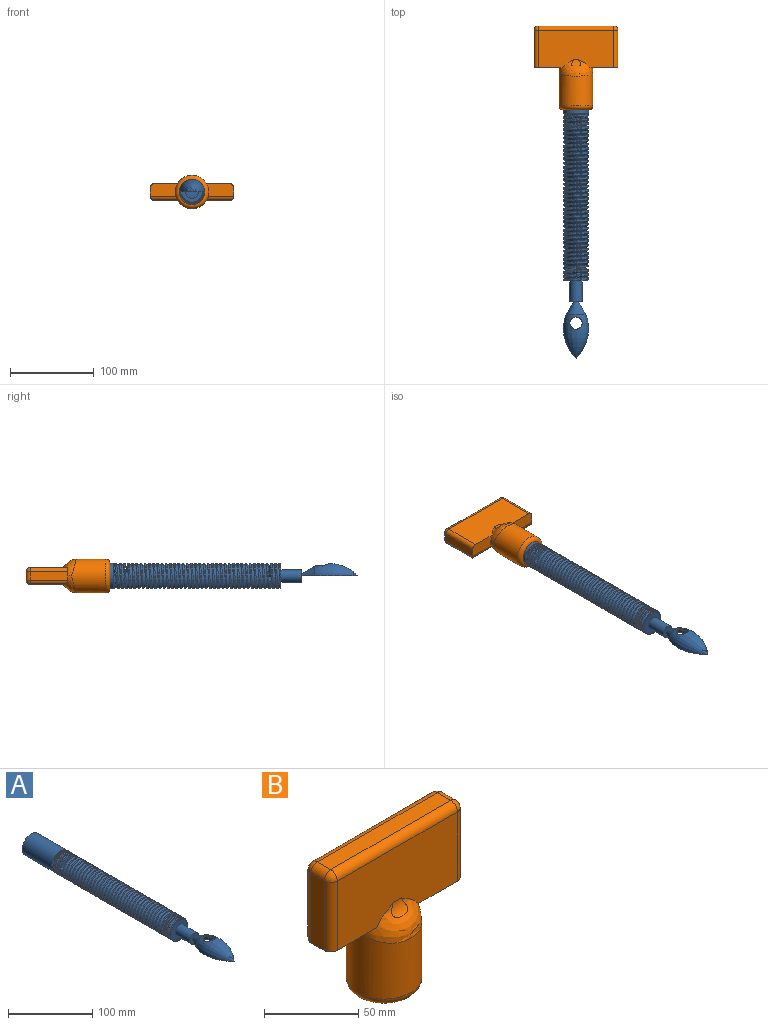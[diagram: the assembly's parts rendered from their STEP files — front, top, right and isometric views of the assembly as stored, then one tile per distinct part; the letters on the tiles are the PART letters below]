
ASSEMBLY  parts=2 mates=2
PART A: 57 faces, bbox 42.2x349.3x47.4 mm
  f0: revolved ~52.11x25.36mm, area 1460.1mm2, adj f53,f54,f55,f56
  f1: revolved ~52.11x29.95mm, area 1804.3mm2, adj f51,f54,f55,f56
  f2: cylinder r=15mm len=20.32mm, axis (0,1,0), area 22.9mm2, adj f3,f43,f46
  f3: cylinder r=15mm len=30mm, axis (0,1,0), area 146.8mm2, adj f2,f4,f45,f46
  f4: cylinder r=15mm len=30mm, axis (0,1,0), area 146.7mm2, adj f3,f5,f45,f46
  f5: cylinder r=15mm len=30mm, axis (0,1,0), area 146.7mm2, adj f4,f6,f45,f46
  f6: cylinder r=15mm len=30mm, axis (0,1,0), area 146.8mm2, adj f5,f7,f45,f46
  f7: cylinder r=15mm len=30mm, axis (0,1,0), area 146.7mm2, adj f6,f8,f45,f46
  f8: cylinder r=15mm len=30mm, axis (0,1,0), area 146.7mm2, adj f7,f9,f45,f46
  f9: cylinder r=15mm len=30mm, axis (0,1,0), area 146.7mm2, adj f8,f10,f45,f46
  f10: cylinder r=15mm len=30mm, axis (0,1,0), area 146.8mm2, adj f9,f11,f45,f46
  f11: cylinder r=15mm len=30mm, axis (0,1,0), area 146.8mm2, adj f10,f12,f45,f46
  f12: cylinder r=15mm len=30mm, axis (0,1,0), area 146.7mm2, adj f11,f13,f45,f46
  f13: cylinder r=15mm len=30mm, axis (0,1,0), area 146.7mm2, adj f12,f14,f45,f46
  f14: cylinder r=15mm len=30mm, axis (0,1,0), area 146.7mm2, adj f13,f15,f45,f46
  f15: cylinder r=15mm len=30mm, axis (0,1,0), area 146.7mm2, adj f14,f16,f45,f46
  f16: cylinder r=15mm len=30mm, axis (0,1,0), area 146.7mm2, adj f15,f17,f45,f46
  f17: cylinder r=15mm len=30mm, axis (0,1,0), area 146.8mm2, adj f16,f18,f45,f46
  f18: cylinder r=15mm len=30mm, axis (0,1,0), area 146.8mm2, adj f17,f19,f45,f46
  f19: cylinder r=15mm len=30mm, axis (0,1,0), area 146.7mm2, adj f18,f20,f45,f46
  f20: cylinder r=15mm len=30mm, axis (0,1,0), area 146.7mm2, adj f19,f21,f45,f46
  f21: cylinder r=15mm len=30mm, axis (0,1,0), area 146.7mm2, adj f20,f22,f45,f46
  f22: cylinder r=15mm len=30mm, axis (0,1,0), area 146.7mm2, adj f21,f23,f45,f46
  f23: cylinder r=15mm len=30mm, axis (0,1,0), area 146.7mm2, adj f22,f24,f45,f46
  f24: cylinder r=15mm len=30mm, axis (0,1,0), area 146.7mm2, adj f23,f25,f45,f46
  f25: cylinder r=15mm len=30mm, axis (0,1,0), area 146.8mm2, adj f24,f26,f45,f46
  f26: cylinder r=15mm len=30mm, axis (0,1,0), area 146.8mm2, adj f25,f27,f45,f46
  f27: cylinder r=15mm len=30mm, axis (0,1,0), area 146.7mm2, adj f26,f28,f45,f46
  f28: cylinder r=15mm len=30mm, axis (0,1,0), area 146.7mm2, adj f27,f29,f45,f46
  f29: cylinder r=15mm len=30mm, axis (0,1,0), area 146.7mm2, adj f28,f30,f45,f46
  f30: cylinder r=15mm len=30mm, axis (0,1,0), area 146.8mm2, adj f29,f31,f45,f46
  f31: cylinder r=15mm len=30mm, axis (0,1,0), area 146.7mm2, adj f30,f32,f45,f46
  f32: cylinder r=15mm len=30mm, axis (0,1,0), area 146.7mm2, adj f31,f33,f45,f46
  f33: cylinder r=15mm len=30mm, axis (0,1,0), area 146.8mm2, adj f32,f34,f45,f46
  f34: cylinder r=15mm len=30mm, axis (0,1,0), area 146.7mm2, adj f33,f35,f45,f46
  f35: cylinder r=15mm len=30mm, axis (0,1,0), area 146.7mm2, adj f34,f36,f45,f46
  f36: cylinder r=15mm len=30mm, axis (0,1,0), area 146.7mm2, adj f35,f37,f45,f46
  f37: cylinder r=15mm len=30mm, axis (0,1,0), area 146.8mm2, adj f36,f38,f45,f46
  f38: cylinder r=15mm len=30mm, axis (0,1,0), area 146.8mm2, adj f37,f39,f45,f46
  f39: cylinder r=15mm len=30mm, axis (0,1,0), area 146.7mm2, adj f38,f40,f45,f46
  f40: cylinder r=15mm len=30mm, axis (0,1,0), area 146.7mm2, adj f39,f41,f45,f46
  f41: cylinder r=15mm len=30mm, axis (0,1,0), area 146.7mm2, adj f40,f42,f45,f46
  f42: cylinder r=15mm len=55mm, axis (0,1,0), area 4850.7mm2, adj f41,f44,f45,f46,f47,f48
  f43: plane 29.77x28.64mm, normal (0,-1,0), area 450.6mm2, adj f2,f45,f46,f49
  f44: plane 2.6x1.22mm, normal (0,-0.05,1), area 2.3mm2, adj f42,f45,f46,f47
  f45: bspline ~206.21x36.37mm, area 13387.7mm2, adj f3,f4,f5,f6,f7,f8,f9,f10
  f46: bspline ~201.04x39.93mm, area 9156.4mm2, adj f2,f3,f4,f5,f6,f7,f8,f9
  f47: plane 29.03x15mm, normal (0,-1,0), area 39.8mm2, adj f42,f44,f45
  f48: plane 30x30mm, normal (0,1,0), area 706.9mm2, adj f42
  f49: cylinder r=7.5mm len=25mm, axis (0,1,0), area 1178.1mm2, adj f43,f50
  f50: plane 15x15mm, normal (0,-1,0), area 171.1mm2, adj f49,f52,f53,f54,f55
  f51: cone r=3.17mm half-angle=29.9deg, axis (0,-1,0), area 390.6mm2, adj f1,f52,f54,f55
  f52: cone r=1.61mm half-angle=86.5deg, axis (0,-1,0), area 5.9mm2, adj f50,f51,f54,f55
  f53: cone r=1.61mm half-angle=29.9deg, axis (0,-1,0), area 311mm2, adj f0,f50,f54,f55
  f54: plane 66.78x14.97mm, normal (0,0,-1), area 118.5mm2, adj f0,f1,f50,f51,f52,f53
  f55: plane 74.26x22.45mm, normal (0,0,-1), area 118.5mm2, adj f0,f1,f50,f51,f52,f53
  f56: cylinder r=7.37mm len=14.74mm, axis (0,0,-1), area 105.2mm2, adj f0,f1
PART B: 30 faces, bbox 101.4x44.6x101.4 mm
  f0: plane 35.03x15.46mm, normal (0,0,-1), area 466.6mm2, adj f4,f5,f10,f11,f17,f27
  f1: plane 35.01x15.43mm, normal (0,0,-1), area 466.6mm2, adj f2,f5,f10,f11,f23,f24
  f2: plane 45x10mm, normal (1,0,0), area 450mm2, adj f1,f21,f23,f25
  f3: plane 90x10mm, normal (0,0,1), area 900mm2, adj f16,f19,f20,f21
  f4: plane 45x10mm, normal (-1,0,0), area 450mm2, adj f0,f17,f19,f28
  f5: plane 90.01x45.01mm, normal (0,-1,0), area 3841.4mm2, adj f0,f1,f8,f11,f16,f17,f23
  f6: plane 91.35x41.35mm, normal (0,1,0), area 3526.9mm2, adj f9,f10,f20,f24,f25,f27,f28
  f7: cylinder r=20mm len=41.02mm, axis (0,0,1), area 4795.7mm2, adj f10,f11,f14
  f8: cylinder r=10mm len=11.2mm, axis (-1,0,0), area 85mm2, adj f5,f11
  f9: cylinder r=10mm len=11.2mm, axis (1,0,0), area 85mm2, adj f6,f10
  f10: bspline ~90.04x35.72mm, area 727.1mm2, adj f0,f1,f6,f7,f9,f11,f24,f27
  f11: bspline ~90.04x35.74mm, area 679mm2, adj f0,f1,f5,f7,f8,f10
  f12: cylinder r=15mm len=30mm, axis (0,0,-1), area 1885mm2, adj f14,f15
  f13: plane 20x20mm, normal (0,0,-1), area 314.2mm2, adj f15
  f14: torus R=15mm, axis (0,0,-1), area 897.3mm2, adj f7,f12
  f15: torus R=10mm, axis (0,0,-1), area 650.6mm2, adj f12,f13
  f16: cylinder r=5mm len=90mm, axis (1,0,0), area 706.9mm2, adj f3,f5,f18,f22
  f17: cylinder r=5mm len=45mm, axis (0,0,1), area 353.4mm2, adj f0,f4,f5,f18
  f18: sphere r=5mm, area 39.3mm2, adj f16,f17,f19
  f19: cylinder r=5mm len=10mm, axis (0,-1,0), area 78.5mm2, adj f3,f4,f18,f29
  f20: cylinder r=5mm len=90mm, axis (-1,0,0), area 706.9mm2, adj f3,f6,f26,f29
  f21: cylinder r=5mm len=10mm, axis (0,1,0), area 78.5mm2, adj f2,f3,f22,f26
  f22: sphere r=5mm, area 39.3mm2, adj f16,f21,f23
  f23: cylinder r=5mm len=45mm, axis (0,0,-1), area 353.4mm2, adj f1,f2,f5,f22
  f24: cylinder r=5mm len=38.89mm, axis (1,0,0), area 256.8mm2, adj f1,f6,f10,f25
  f25: cylinder r=5mm len=45mm, axis (0,0,1), area 333.8mm2, adj f2,f6,f24,f26
  f26: sphere r=5mm, area 25mm2, adj f20,f21,f25
  f27: cylinder r=5mm len=38.89mm, axis (1,0,0), area 256.8mm2, adj f0,f6,f10,f28
  f28: cylinder r=5mm len=45mm, axis (0,0,-1), area 333.8mm2, adj f4,f6,f27,f29
  f29: sphere r=5mm, area 39.3mm2, adj f19,f20,f28
PLACE A rot(axis=(0,0.02,1),0deg) t=(271.02,350.8,55.35)mm
PLACE B rot(axis=(-1,0,0),90deg) t=(271.02,429.53,45.35)mm
MATE slider B.f15 <-> A.f2  axis (0,-1,0) through (271.02,364.53,55.35)mm
MATE fastened A.f2 <-> B.f12  axis (0,1,0) through (271.02,400.8,55.35)mm
